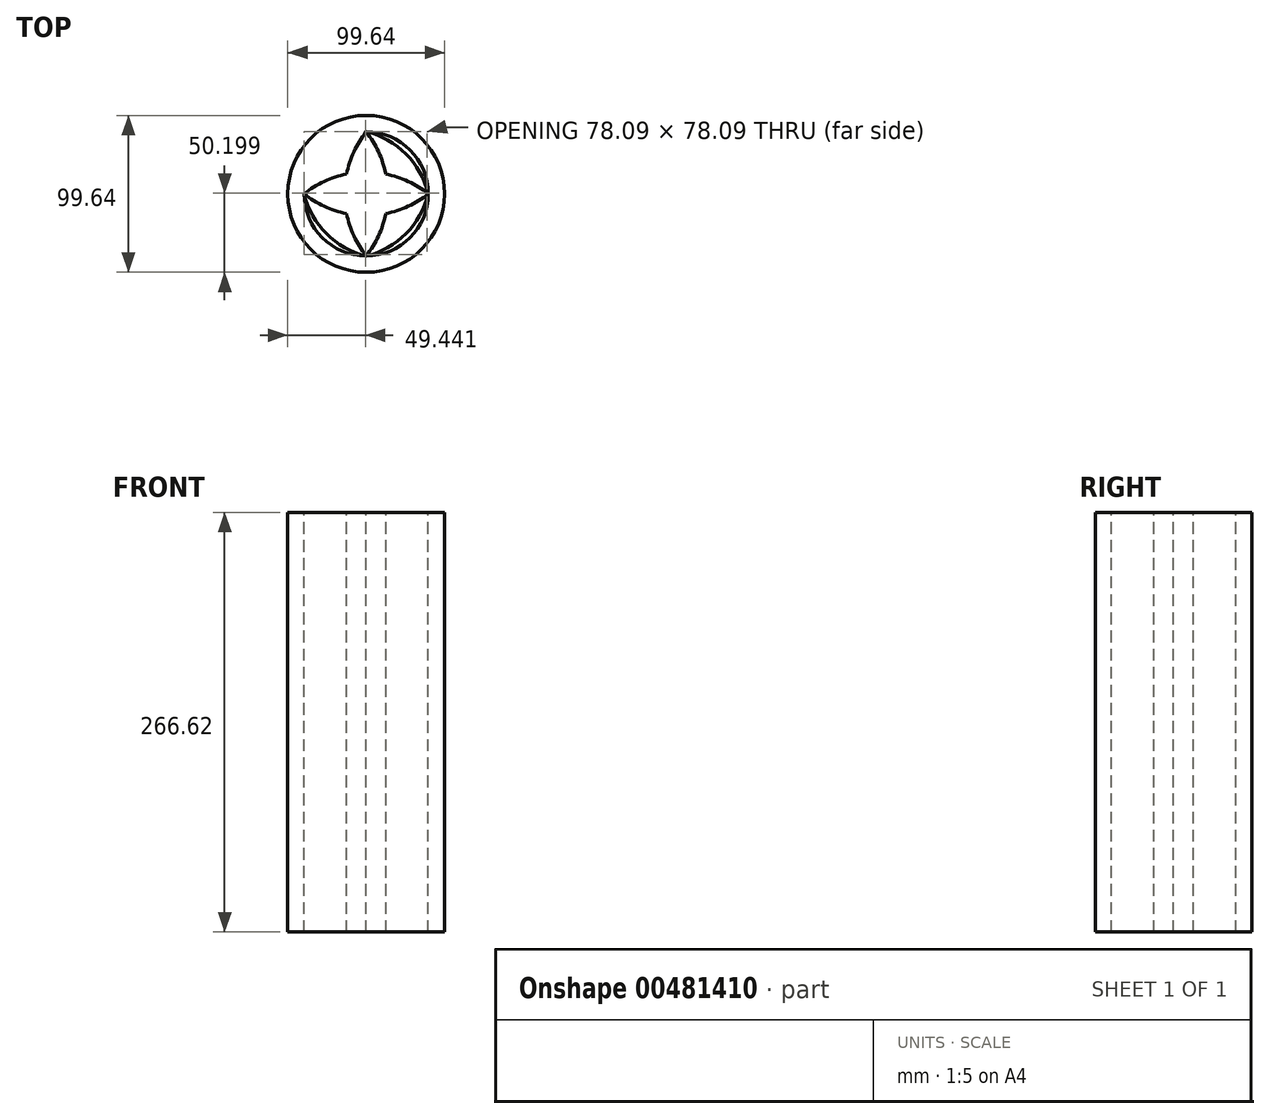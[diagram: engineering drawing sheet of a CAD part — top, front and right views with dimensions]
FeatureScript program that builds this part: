
annotation { "Feature Type Name" : "Feature", "Feature Type Description" : "" }
export const myFeature = defineFeature(function(context is Context, id is Id, definition is map)
    precondition{}
    {
        {
            var Q0;
            Q0=qCreatedBy(makeId("Top.planeOp"),FACE);
            var sketch = newSketch(context, id + "F0", { "sketchPlane" : qUnion([Q0])});
            skCircle(sketch, "E0", {"center": v(0, 0) * mm, "radius": 49.82 * mm});
            skArc(sketch, "E1", {"start": v(39.42, 0) * mm, "mid": v(0, -39.42) * mm, "end": v(-39.42, 0) * mm});
            skArc(sketch, "E2", {"start": v(-39.42, 0) * mm, "mid": v(0, 13.71) * mm, "end": v(39.42, 0) * mm});
            skArc(sketch, "E3", {"start": v(-39.42, 0) * mm, "mid": v(0, -13.71) * mm, "end": v(39.42, 0) * mm});
            skArc(sketch, "E4", {"start": v(-39.42, 0) * mm, "mid": v(0, 39.42) * mm, "end": v(39.42, 0) * mm});
            skArc(sketch, "E5", {"start": v(0, -39.42) * mm, "mid": v(-13.71, 0) * mm, "end": v(0, 39.42) * mm});
            skArc(sketch, "E6", {"start": v(0, 39.42) * mm, "mid": v(13.71, 0) * mm, "end": v(0, -39.42) * mm});
            skArc(sketch, "E7", {"start": v(-39.42, 0) * mm, "mid": v(-25.27, -25.27) * mm, "end": v(0, -39.42) * mm});
            skArc(sketch, "E8", {"start": v(0, -39.42) * mm, "mid": v(25.27, -25.27) * mm, "end": v(39.42, 0) * mm});
            skArc(sketch, "E9", {"start": v(39.42, 0) * mm, "mid": v(25.27, 25.27) * mm, "end": v(0, 39.42) * mm});
            skArc(sketch, "E10", {"start": v(-39.42, 0) * mm, "mid": v(-25.27, 25.27) * mm, "end": v(0, 39.42) * mm});
            skSolve(sketch);
        }
        {
            var Q0;
            Q0=makeQuery(id+"F0.imprint","IMPRINT",FACE,{"disambiguationData":[TD([[makeQuery(id+"F0.imprint","IMPRINT",EDGE,{"derivedFrom":sQuery(id+"F0.wireOp",EDGE,"E0")}),1.0]])]});
            var Q1;
            {var subQ0=sQuery(id+"F0.wireOp",EDGE,"E8");Q1=makeQuery(id+"F0.imprint","IMPRINT",FACE,{"disambiguationData":[TD([[makeQuery(id+"F0.imprint","IMPRINT",EDGE,{"derivedFrom":subQ0}),1.0]])]});}
            var Q2;
            {var subQ0=sQuery(id+"F0.wireOp",EDGE,"E9");Q2=makeQuery(id+"F0.imprint","IMPRINT",FACE,{"disambiguationData":[TD([[makeQuery(id+"F0.imprint","IMPRINT",EDGE,{"derivedFrom":subQ0}),1.0]])]});}
            var Q3;
            {var subQ0=sQuery(id+"F0.wireOp",EDGE,"E10");Q3=makeQuery(id+"F0.imprint","IMPRINT",FACE,{"disambiguationData":[TD([[makeQuery(id+"F0.imprint","IMPRINT",EDGE,{"derivedFrom":subQ0}),-1.0]])]});}
            var Q4;
            {var subQ0=sQuery(id+"F0.wireOp",EDGE,"E7");Q4=makeQuery(id+"F0.imprint","IMPRINT",FACE,{"disambiguationData":[TD([[makeQuery(id+"F0.imprint","IMPRINT",EDGE,{"derivedFrom":subQ0}),1.0]])]});}
            var Q5;
            {var subQ0=sQuery(id+"F0.wireOp",EDGE,"E5");var subQ1=sQuery(id+"F0.wireOp",EDGE,"E2");var subQ2=makeQuery(id+"F0.imprint","INTERSECT",VERTEX,{"derivedFrom":[subQ1,subQ0]});Q5=makeQuery(id+"F0.imprint","IMPRINT",FACE,{"disambiguationData":[TD([[makeQuery(id+"F0.imprint","IMPRINT",EDGE,{"disambiguationData":[TD([[subQ2,-1.0]])],"derivedFrom":subQ1}),-1.0]])]});}
            extrude(context, id + "F1", {"entities" : qUnion([Q0, Q1, Q2, Q3, Q4, Q5]), "oppositeDirection" : true, "depth" : 266.62 * mm});
        }
    });
